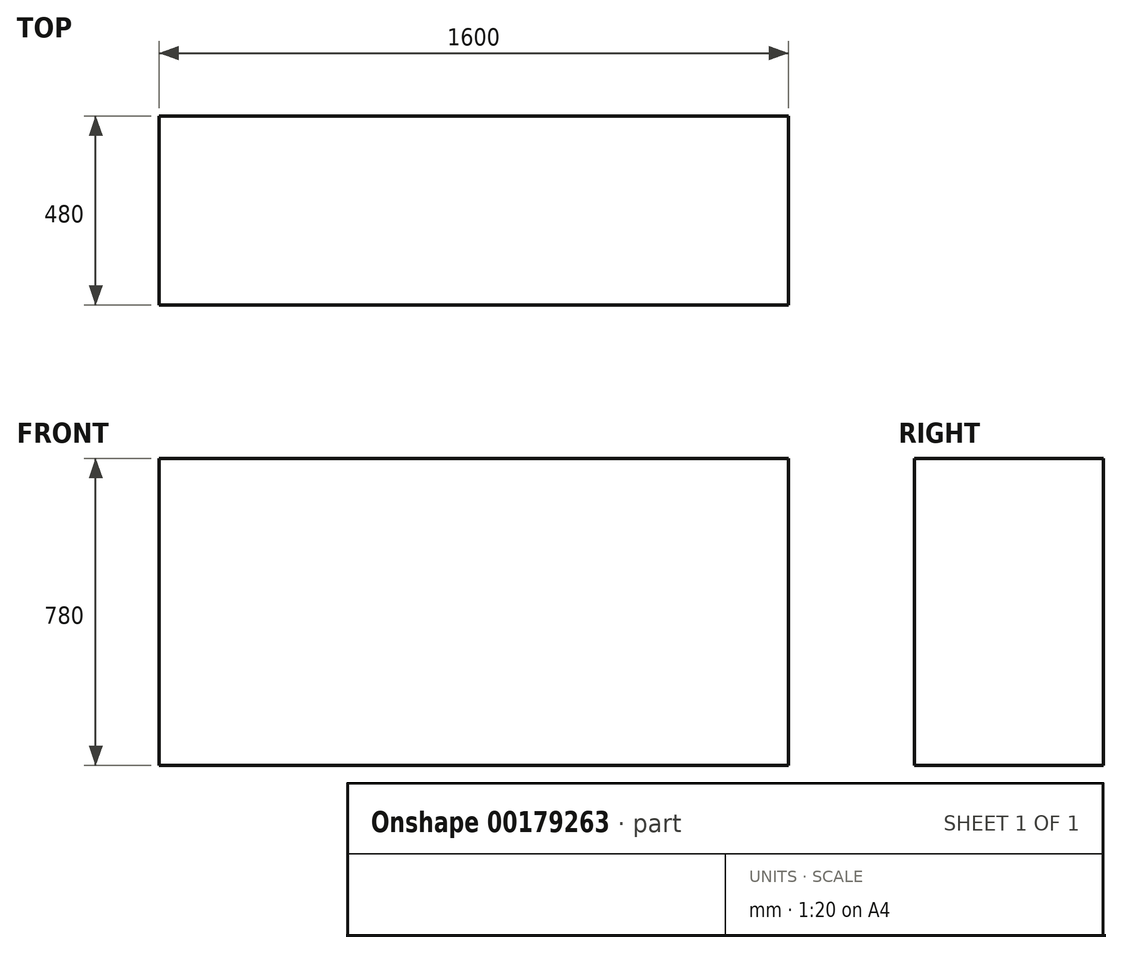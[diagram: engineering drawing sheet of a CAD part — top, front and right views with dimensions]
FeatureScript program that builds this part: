
annotation { "Feature Type Name" : "Feature", "Feature Type Description" : "" }
export const myFeature = defineFeature(function(context is Context, id is Id, definition is map)
    precondition{}
    {
        {
            var Q0;
            Q0=qCreatedBy(makeId("Top.planeOp"),FACE);
            var sketch = newSketch(context, id + "F0", { "sketchPlane" : qUnion([Q0])});
            skLineSegment(sketch, "E0.bottom", {"start": v(0, 0) * mm, "end": v(1600, 0) * mm});
            skLineSegment(sketch, "E0.top", {"start": v(0, 480) * mm, "end": v(1600, 480) * mm});
            skLineSegment(sketch, "E0.left", {"start": v(0, 0) * mm, "end": v(0, 480) * mm});
            skLineSegment(sketch, "E0.right", {"start": v(1600, 0) * mm, "end": v(1600, 480) * mm});
            skSolve(sketch);
        }
        {
            var Q0;
            Q0 = qSketchRegion(id + "F0", true);
            extrude(context, id + "F1", {"entities" : qUnion([Q0]), "depth" : 780 * mm});
        }
    });
